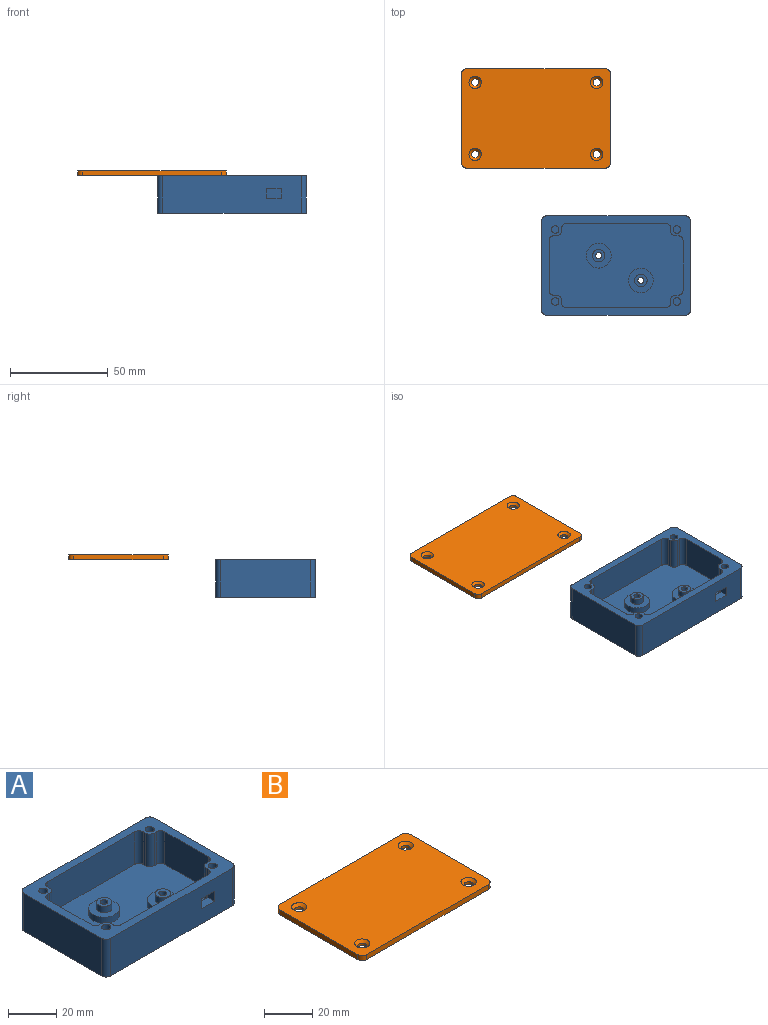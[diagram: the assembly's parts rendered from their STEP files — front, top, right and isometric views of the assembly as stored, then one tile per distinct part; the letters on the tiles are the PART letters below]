
ASSEMBLY  parts=2 mates=1
PART A: 71 faces, bbox 76.2x50.8x19.1 mm
  f0: plane 76.2x50.8mm, normal (0,0,-1), area 3790mm2, adj f7,f8,f9,f10,f37,f38,f39,f40
  f1: plane 68.58x43.18mm, normal (0,0,1), area 2541.1mm2, adj f2,f3,f4,f5,f11,f12,f13,f14
  f2: plane 25.4x16.51mm, normal (1,0,0), area 419.4mm2, adj f1,f6,f55,f59
  f3: plane 25.4x16.51mm, normal (-1,0,0), area 419.4mm2, adj f1,f6,f51,f61
  f4: plane 50.8x16.51mm, normal (0,-1,0), area 838.7mm2, adj f1,f6,f53,f56
  f5: plane 50.8x16.51mm, normal (0,1,0), area 800mm2, adj f1,f6,f57,f62,f67,f68,f69,f70
  f6: plane 76.2x50.8mm, normal (0,0,1), area 1025.4mm2, adj f2,f3,f4,f5,f7,f8,f9,f10
  f7: plane 45.72x19.05mm, normal (-1,0,0), area 871mm2, adj f0,f6,f63,f66
  f8: plane 71.12x19.05mm, normal (0,-1,0), area 1316.1mm2, adj f0,f6,f63,f64,f67,f68,f69,f70
  f9: plane 45.72x19.05mm, normal (1,0,0), area 871mm2, adj f0,f6,f64,f65
  f10: plane 71.12x19.05mm, normal (0,1,0), area 1354.8mm2, adj f0,f6,f65,f66
  f11: plane 16.51x1.27mm, normal (-1,0,0), area 21mm2, adj f1,f6,f60,f62
  f12: plane 16.51x1.27mm, normal (0,1,0), area 21mm2, adj f1,f6,f60,f61
  f13: plane 16.51x1.27mm, normal (-1,0,0), area 21mm2, adj f1,f6,f52,f53
  f14: plane 16.51x1.27mm, normal (0,-1,0), area 21mm2, adj f1,f6,f51,f52
  f15: plane 16.51x1.27mm, normal (1,0,0), area 21mm2, adj f1,f6,f57,f58
  f16: plane 16.51x1.27mm, normal (0,1,0), area 21mm2, adj f1,f6,f58,f59
  f17: plane 16.51x1.27mm, normal (1,0,0), area 21mm2, adj f1,f6,f54,f56
  f18: plane 16.51x1.27mm, normal (0,-1,0), area 21mm2, adj f1,f6,f54,f55
  f19: cylinder r=1.91mm len=8.89mm, axis (0,0,1), area 106.4mm2, adj f6,f20
  f20: plane 3.81x3.81mm, normal (0,0,1), area 11.4mm2, adj f19
  f21: cylinder r=1.91mm len=8.89mm, axis (0,0,1), area 106.4mm2, adj f6,f22
  f22: plane 3.81x3.81mm, normal (0,0,1), area 11.4mm2, adj f21
  f23: cylinder r=1.91mm len=8.89mm, axis (0,0,1), area 106.4mm2, adj f6,f24
  f24: plane 3.81x3.81mm, normal (0,0,1), area 11.4mm2, adj f23
  f25: cylinder r=1.91mm len=8.89mm, axis (0,0,1), area 106.4mm2, adj f6,f26
  f26: plane 3.81x3.81mm, normal (0,0,1), area 11.4mm2, adj f25
  f27: cylinder r=1.59mm len=5.08mm, axis (0,0,-1), area 50.7mm2, adj f29,f50
  f28: cylinder r=3.17mm len=6.35mm, axis (0,0,-1), area 63.3mm2, adj f29,f34
  f29: plane 6.35x6.35mm, normal (0,0,1), area 23.8mm2, adj f27,f28
  f30: cylinder r=1.59mm len=5.08mm, axis (0,0,-1), area 50.7mm2, adj f32,f43
  f31: cylinder r=3.17mm len=6.35mm, axis (0,0,-1), area 63.3mm2, adj f32,f36
  f32: plane 6.35x6.35mm, normal (0,0,1), area 23.8mm2, adj f30,f31
  f33: cylinder r=6.35mm len=12.7mm, axis (0,0,-1), area 126.7mm2, adj f1,f34
  f34: plane 12.7x12.7mm, normal (0,0,1), area 95mm2, adj f28,f33
  f35: cylinder r=6.35mm len=12.7mm, axis (0,0,-1), area 126.7mm2, adj f1,f36
  f36: plane 12.7x12.7mm, normal (0,0,1), area 95mm2, adj f31,f35
  f37: plane 3.81x3.3mm, normal (0.87,-0.5,0), area 14.5mm2, adj f0,f38,f42,f43
  f38: plane 3.81x3.81mm, normal (0,-1,0), area 14.5mm2, adj f0,f37,f39,f43
  f39: plane 3.81x3.3mm, normal (-0.87,-0.5,0), area 14.5mm2, adj f0,f38,f40,f43
  f40: plane 3.81x3.3mm, normal (-0.87,0.5,0), area 14.5mm2, adj f0,f39,f41,f43
  f41: plane 3.81x3.81mm, normal (0,1,0), area 14.5mm2, adj f0,f40,f42,f43
  f42: plane 3.81x3.3mm, normal (0.87,0.5,0), area 14.5mm2, adj f0,f37,f41,f43
  f43: plane 7.62x6.6mm, normal (0,0,-1), area 29.8mm2, adj f30,f37,f38,f39,f40,f41,f42
  f44: plane 3.81x3.3mm, normal (0.87,-0.5,0), area 14.5mm2, adj f0,f45,f49,f50
  f45: plane 3.81x3.81mm, normal (0,-1,0), area 14.5mm2, adj f0,f44,f46,f50
  f46: plane 3.81x3.3mm, normal (-0.87,-0.5,0), area 14.5mm2, adj f0,f45,f47,f50
  f47: plane 3.81x3.3mm, normal (-0.87,0.5,0), area 14.5mm2, adj f0,f46,f48,f50
  f48: plane 3.81x3.81mm, normal (0,1,0), area 14.5mm2, adj f0,f47,f49,f50
  f49: plane 3.81x3.3mm, normal (0.87,0.5,0), area 14.5mm2, adj f0,f44,f48,f50
  f50: plane 7.62x6.6mm, normal (0,0,-1), area 29.8mm2, adj f27,f44,f45,f46,f47,f48,f49
  f51: cylinder r=2.54mm len=16.51mm, axis (0,0,1), area 65.9mm2, adj f1,f3,f6,f14
  f52: cylinder r=2.54mm len=16.51mm, axis (0,0,1), area 65.9mm2, adj f1,f6,f13,f14
  f53: cylinder r=2.54mm len=16.51mm, axis (0,0,1), area 65.9mm2, adj f1,f4,f6,f13
  f54: cylinder r=2.54mm len=16.51mm, axis (0,0,1), area 65.9mm2, adj f1,f6,f17,f18
  f55: cylinder r=2.54mm len=16.51mm, axis (0,0,1), area 65.9mm2, adj f1,f2,f6,f18
  f56: cylinder r=2.54mm len=16.51mm, axis (0,0,-1), area 65.9mm2, adj f1,f4,f6,f17
  f57: cylinder r=2.54mm len=16.51mm, axis (0,0,-1), area 65.9mm2, adj f1,f5,f6,f15
  f58: cylinder r=2.54mm len=16.51mm, axis (0,0,1), area 65.9mm2, adj f1,f6,f15,f16
  f59: cylinder r=2.54mm len=16.51mm, axis (0,0,-1), area 65.9mm2, adj f1,f2,f6,f16
  f60: cylinder r=2.54mm len=16.51mm, axis (0,0,1), area 65.9mm2, adj f1,f6,f11,f12
  f61: cylinder r=2.54mm len=16.51mm, axis (0,0,-1), area 65.9mm2, adj f1,f3,f6,f12
  f62: cylinder r=2.54mm len=16.51mm, axis (0,0,1), area 65.9mm2, adj f1,f5,f6,f11
  f63: cylinder r=2.54mm len=19.05mm, axis (0,0,-1), area 76mm2, adj f0,f6,f7,f8
  f64: cylinder r=2.54mm len=19.05mm, axis (0,0,1), area 76mm2, adj f0,f6,f8,f9
  f65: cylinder r=2.54mm len=19.05mm, axis (0,0,-1), area 76mm2, adj f0,f6,f9,f10
  f66: cylinder r=2.54mm len=19.05mm, axis (0,0,1), area 76mm2, adj f0,f6,f7,f10
  f67: plane 5.08x3.81mm, normal (-1,0,0), area 19.4mm2, adj f5,f8,f68,f70
  f68: plane 7.62x3.81mm, normal (0,0,-1), area 29mm2, adj f5,f8,f67,f69
  f69: plane 5.08x3.81mm, normal (1,0,0), area 19.4mm2, adj f5,f8,f68,f70
  f70: plane 7.62x3.81mm, normal (0,0,1), area 29mm2, adj f5,f8,f67,f69
PART B: 18 faces, bbox 76.2x50.8x2.5 mm
  f0: plane 71.12x2.54mm, normal (0,1,0), area 180.6mm2, adj f4,f5,f14,f17
  f1: plane 45.72x2.54mm, normal (-1,0,0), area 116.1mm2, adj f4,f5,f14,f15
  f2: plane 71.12x2.54mm, normal (0,-1,0), area 180.6mm2, adj f4,f5,f15,f16
  f3: plane 45.72x2.54mm, normal (1,0,0), area 116.1mm2, adj f4,f5,f16,f17
  f4: plane 76.2x50.8mm, normal (0,0,1), area 3738.7mm2, adj f0,f1,f2,f3,f10,f11,f12,f13
  f5: plane 76.2x50.8mm, normal (0,0,-1), area 3819.8mm2, adj f0,f1,f2,f3,f6,f7,f8,f9
  f6: cylinder r=1.91mm len=3.81mm, axis (0,0,1), area 15.2mm2, adj f5,f13
  f7: cylinder r=1.91mm len=3.81mm, axis (0,0,1), area 15.2mm2, adj f5,f12
  f8: cylinder r=1.91mm len=3.81mm, axis (0,0,1), area 15.2mm2, adj f5,f11
  f9: cylinder r=1.91mm len=3.81mm, axis (0,0,1), area 15.2mm2, adj f5,f10
  f10: cone r=1.91mm half-angle=45deg, axis (0,0,1), area 28.7mm2, adj f4,f9
  f11: cone r=1.91mm half-angle=45deg, axis (0,0,1), area 28.7mm2, adj f4,f8
  f12: cone r=1.91mm half-angle=45deg, axis (0,0,1), area 28.7mm2, adj f4,f7
  f13: cone r=1.91mm half-angle=45deg, axis (0,0,1), area 28.7mm2, adj f4,f6
  f14: cylinder r=2.54mm len=2.54mm, axis (0,0,-1), area 10.1mm2, adj f0,f1,f4,f5
  f15: cylinder r=2.54mm len=2.54mm, axis (0,0,1), area 10.1mm2, adj f1,f2,f4,f5
  f16: cylinder r=2.54mm len=2.54mm, axis (0,0,-1), area 10.1mm2, adj f2,f3,f4,f5
  f17: cylinder r=2.54mm len=2.54mm, axis (0,0,1), area 10.1mm2, adj f0,f3,f4,f5
PLACE A t=(8.72,-15.44,136.53)mm
PLACE B t=(-30.66,-8.1,155.58)mm
MATE planar B.f5 <-> A.f6  axis (0,0,-1) through (44.02,74.3,155.58)mm
